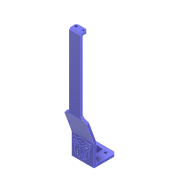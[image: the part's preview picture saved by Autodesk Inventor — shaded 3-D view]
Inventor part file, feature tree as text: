
AUTODESK INVENTOR PART (.ipt)
format: ipt  version: 2022 (Build 260153000, 153)  size: 636,416 bytes
history: native  units: mm
features: sketch x11, extrude x6, hole x3, other x3, chamfer x2, rib x1, mirror x1
ambient origin geometry x8: Origin, YZ Plane, XZ Plane, XY Plane, X Axis, Y Axis, Z Axis, Center Point
bodies: Solid1 (feature_tree)
feature tree (27):
  extrude  "Extrusion1"  Depth=30.0mm
  extrude  "Extrusion2"  Depth=3.0mm
  hole  "Mounting Holes"  [1 undecoded]
  rib  "Rib1"
  mirror  "Mirror1"
  other  "Bend Part1"
  hole  "Camera Mounting Holes"  [1 undecoded]
  chamfer  "Chamfer1"  Distance=3.0mm
  extrude  "Decepticon Logo"  Depth=15.0mm
  extrude  "Autobots Logo"  Depth=6.0mm
  extrude  "Compass Mount"  Depth=27.0mm
  extrude  "Extrusion7"  Depth=32.0mm
  hole  "Compass Mount Holes"  [1 undecoded]
  chamfer  "Chamfer3"  Distance=2.0mm
  sketch  "Sketch1"  dims[d0=30.0mm d1=30.0mm]
  sketch  "Sketch2"  dims[d2=3.0mm d3=0.0mm d4=21.0mm]
  sketch  "Sketch5"  dims[d5=13.0mm]
  sketch  "Sketch6"  dims[d7=2.4mm d8=6.0mm d9=4.0mm d10=2.0mm d11=90.0deg d12=6.0mm d13=0.0mm d15=30.0mm]
  sketch  "Sketch7"  dims[d16=30.0mm d17=3.0mm]
  sketch  "Sketch8"  dims[d18=3.0mm d19=3.0mm d20=0.0mm]
  other  "Image1"
  sketch  "Sketch10"  dims[d21=15.0mm d22=13.5mm]
  other  "Image2"
  sketch  "Sketch12"  dims[d23=7.0mm]
  sketch  "Sketch13"  dims[d24=3.4mm d25=6.0mm d26=4.0mm d27=2.0mm d28=90.0deg d29=6.0mm d30=0.0mm d31=22.0mm]
  sketch  "Sketch14"  dims[d35=1.0mm]
  sketch  "Sketch15"  dims[d36=2.0mm d37=0.0mm d38=0.0mm d39=1.0mm d40=1.0mm d41=27.0mm d42=32.0mm d43=3.0mm d44=2.0mm d45=45.0deg d71=2.0mm d72=0.0mm d157=2.0mm d158=0.0mm d162=3.0mm d163=3.490659mm d164=4.0mm d167=100.0mm d168=15.0mm d169=0.0mm d170=7.0mm d171=3.0mm d172=0.0mm d173=2.0mm d174=2.0mm d175=45.0deg d176=9.5mm d177=3.4mm d178=6.0mm d179=4.0mm d180=2.0mm d181=90.0deg d182=8.0mm d183=20.594885mm d184=3.0mm d185=2.0mm d186=45.0deg d73=0.5mm d74=0.872665mm]
note: 3 required parameter values undecoded (feature->parameter linkage not recoverable at this tier; creation-order binding heuristic only, values carry confidence <= 0.55)
